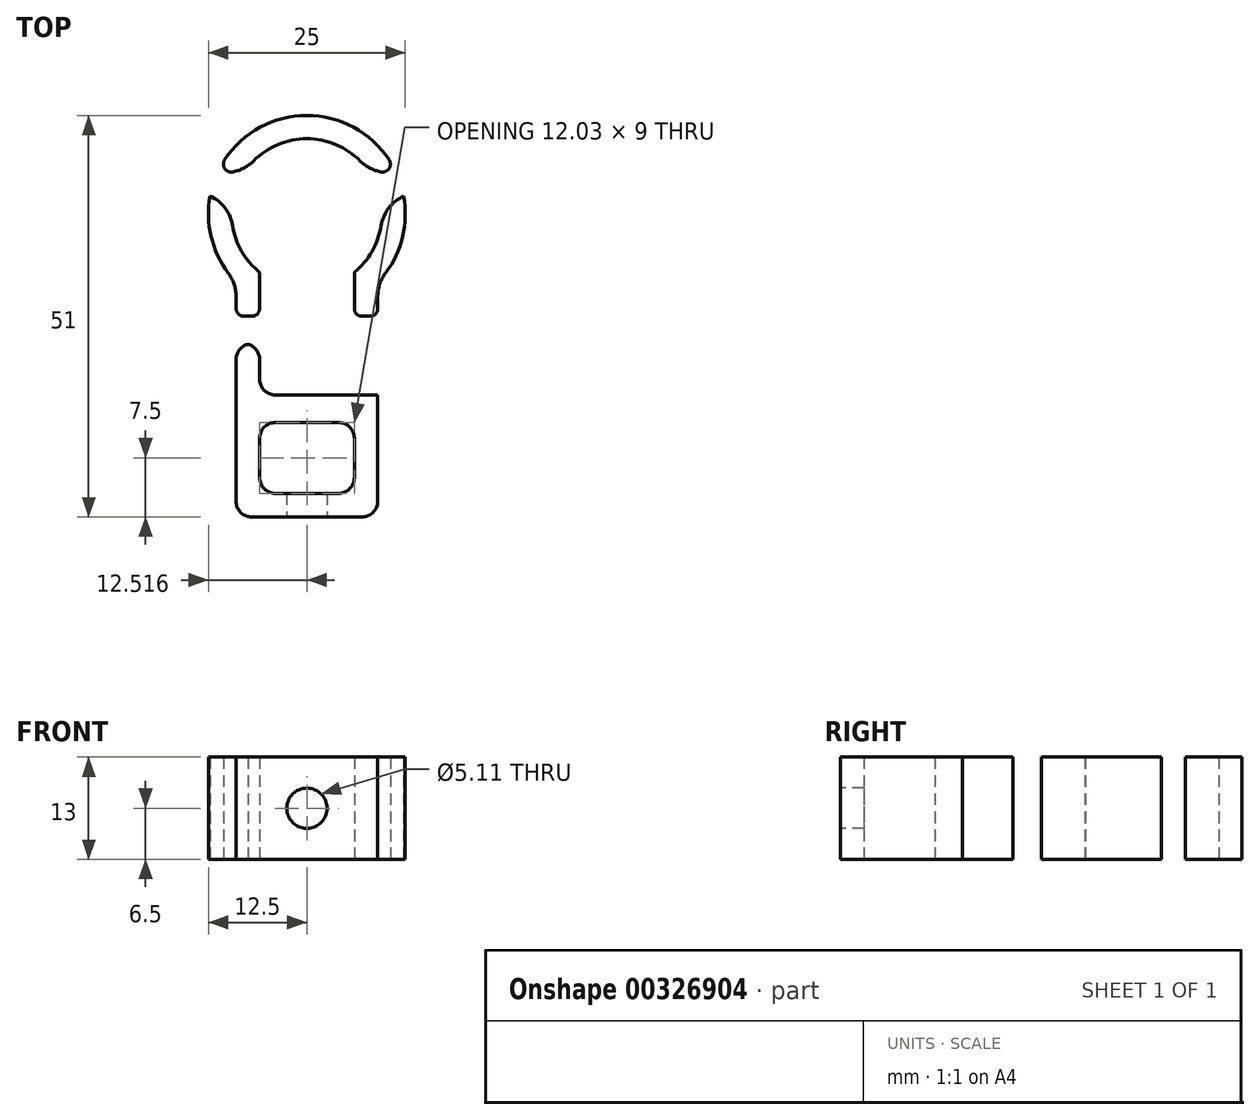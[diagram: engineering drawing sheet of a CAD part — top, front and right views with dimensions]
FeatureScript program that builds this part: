
annotation { "Feature Type Name" : "Feature", "Feature Type Description" : "" }
export const myFeature = defineFeature(function(context is Context, id is Id, definition is map)
    precondition{}
    {
        {
            var Q0;
            Q0=qCreatedBy(makeId("Top.planeOp"),FACE);
            var sketch = newSketch(context, id + "F0", { "sketchPlane" : qUnion([Q0])});
            skCircle(sketch, "E0", {"center": v(0, 0) * mm, "radius": 9.55 * mm});
            skCircle(sketch, "E1", {"center": v(0, 0) * mm, "radius": 12.5 * mm});
            skLineSegment(sketch, "E2", {"start": v(-6, -16.5) * mm, "end": v(-6, -10.97) * mm});
            skLineSegment(sketch, "E3", {"start": v(6.03, -16.54) * mm, "end": v(6.03, -10.95) * mm});
            skLineSegment(sketch, "E4", {"start": v(-12.3, 2.26) * mm, "end": v(12.3, 2.26) * mm});
            skLineSegment(sketch, "E5.0", {"start": v(-12.3, 5.26) * mm, "end": v(12.3, 5.26) * mm});
            skLineSegment(sketch, "E6", {"start": v(6.03, -10.95) * mm, "end": v(6.03, -7.4) * mm});
            skLineSegment(sketch, "E7", {"start": v(-6, -10.97) * mm, "end": v(-6, -7.43) * mm});
            skLineSegment(sketch, "E8", {"start": v(-6, -7.43) * mm, "end": v(-6, -16.5) * mm});
            skLineSegment(sketch, "E9", {"start": v(6.03, -7.4) * mm, "end": v(6.03, -16.54) * mm});
            skLineSegment(sketch, "E10.0", {"start": v(-9, -16.5) * mm, "end": v(-9, -10.97) * mm});
            skLineSegment(sketch, "E11", {"start": v(-9, -10.97) * mm, "end": v(-9, -8.67) * mm});
            skLineSegment(sketch, "E12", {"start": v(9, -16.5) * mm, "end": v(9, -8.67) * mm});
            skLineSegment(sketch, "E13", {"start": v(-9, -16.5) * mm, "end": v(9, -16.5) * mm});
            skLineSegment(sketch, "E14.0", {"start": v(-9, -13) * mm, "end": v(9, -13) * mm});
            skLineSegment(sketch, "E15", {"start": v(-6, -7.43) * mm, "end": v(6.03, -7.4) * mm});
            skLineSegment(sketch, "E16.0", {"start": v(-6.02, -6.43) * mm, "end": v(6.05, -6.4) * mm});
            skLineSegment(sketch, "E17", {"start": v(6.05, -6.4) * mm, "end": v(7.08, -6.4) * mm});
            skLineSegment(sketch, "E18", {"start": v(-6.02, -6.43) * mm, "end": v(-7.06, -6.43) * mm});
            skLineSegment(sketch, "E19.0", {"start": v(-9, -26.5) * mm, "end": v(9, -26.5) * mm});
            skLineSegment(sketch, "E20", {"start": v(-9, -16.5) * mm, "end": v(-9, -26.5) * mm});
            skLineSegment(sketch, "E21", {"start": v(9, -16.5) * mm, "end": v(9, -26.5) * mm});
            skLineSegment(sketch, "E22", {"start": v(6.03, -16.54) * mm, "end": v(6.03, -26.5) * mm});
            skLineSegment(sketch, "E23", {"start": v(-6, -16.5) * mm, "end": v(-6, -26.5) * mm});
            skLineSegment(sketch, "E24.0", {"start": v(-9, -23) * mm, "end": v(9, -23) * mm});
            skLineSegment(sketch, "E25.0", {"start": v(-9, -35.5) * mm, "end": v(9, -35.5) * mm});
            skLineSegment(sketch, "E26.0", {"start": v(-9, -38.5) * mm, "end": v(9, -38.5) * mm});
            skLineSegment(sketch, "E27", {"start": v(-9, -38.5) * mm, "end": v(-9, -26.5) * mm});
            skLineSegment(sketch, "E28", {"start": v(9, -38.5) * mm, "end": v(9, -26.5) * mm});
            skLineSegment(sketch, "E29", {"start": v(6.03, -26.5) * mm, "end": v(6.03, -35.5) * mm});
            skLineSegment(sketch, "E30", {"start": v(-6, -26.5) * mm, "end": v(-6, -35.5) * mm});
            skSolve(sketch);
        }
        {
            var Q0;
            {var subQ0=sQuery(id+"F0.wireOp",EDGE,"E5.0");var subQ1=sQuery(id+"F0.wireOp",EDGE,"E0");var subQ2=makeQuery(id+"F0.imprint","INTERSECT",VERTEX,{"disambiguationData":[OD(1.0)],"derivedFrom":[subQ1,subQ0]});Q0=makeQuery(id+"F0.imprint","IMPRINT",FACE,{"disambiguationData":[TD([[makeQuery(id+"F0.imprint","IMPRINT",EDGE,{"disambiguationData":[TD([[subQ2,-1.0]])],"derivedFrom":subQ1}),-1.0]])]});}
            var Q1;
            {var subQ2=sQuery(id+"F0.wireOp",EDGE,"E8");var subQ6=sQuery(id+"F0.wireOp",EDGE,"E0");var subQ8=makeQuery(id+"F0.imprint","INTERSECT",VERTEX,{"derivedFrom":[subQ6,subQ2]});Q1=makeQuery(id+"F0.imprint","IMPRINT",FACE,{"disambiguationData":[TD([[makeQuery(id+"F0.imprint","IMPRINT",EDGE,{"disambiguationData":[TD([[subQ8,1.0]])],"derivedFrom":subQ6}),-1.0]])]});}
            var Q2;
            {var subQ0=sQuery(id+"F0.wireOp",EDGE,"E5.0");var subQ1=sQuery(id+"F0.wireOp",EDGE,"E0");var subQ2=makeQuery(id+"F0.imprint","INTERSECT",VERTEX,{"disambiguationData":[OD(0.0)],"derivedFrom":[subQ1,subQ0]});Q2=makeQuery(id+"F0.imprint","IMPRINT",FACE,{"disambiguationData":[TD([[makeQuery(id+"F0.imprint","IMPRINT",EDGE,{"disambiguationData":[TD([[subQ2,1.0]])],"derivedFrom":subQ1}),-1.0]])]});}
            var Q3;
            {var subQ3=sQuery(id+"F0.wireOp",EDGE,"E0");var subQ5=sQuery(id+"F0.wireOp",EDGE,"E9");var subQ6=makeQuery(id+"F0.imprint","INTERSECT",VERTEX,{"derivedFrom":[subQ3,subQ5]});Q3=makeQuery(id+"F0.imprint","IMPRINT",FACE,{"disambiguationData":[TD([[makeQuery(id+"F0.imprint","IMPRINT",EDGE,{"disambiguationData":[TD([[subQ6,-1.0]])],"derivedFrom":subQ3}),-1.0]])]});}
            var Q4;
            {var subQ0=sQuery(id+"F0.wireOp",EDGE,"E12");var subQ1=sQuery(id+"F0.wireOp",EDGE,"E1");var subQ2=makeQuery(id+"F0.imprint","INTERSECT",VERTEX,{"derivedFrom":[subQ1,subQ0]});Q4=makeQuery(id+"F0.imprint","IMPRINT",FACE,{"disambiguationData":[TD([[makeQuery(id+"F0.imprint","IMPRINT",EDGE,{"disambiguationData":[TD([[subQ2,1.0]])],"derivedFrom":subQ1}),-1.0]])]});}
            var Q5;
            {var subQ0=sQuery(id+"F0.wireOp",EDGE,"E13");var subQ1=sQuery(id+"F0.wireOp",EDGE,"E9");var subQ2=makeQuery(id+"F0.imprint","INTERSECT",VERTEX,{"derivedFrom":[subQ1,subQ0]});Q5=makeQuery(id+"F0.imprint","IMPRINT",FACE,{"disambiguationData":[TD([[makeQuery(id+"F0.imprint","IMPRINT",EDGE,{"disambiguationData":[TD([[subQ2,1.0]])],"derivedFrom":subQ1}),1.0]])]});}
            var Q6;
            {var subQ0=sQuery(id+"F0.wireOp",EDGE,"E13");var subQ1=sQuery(id+"F0.wireOp",EDGE,"E8");var subQ2=makeQuery(id+"F0.imprint","INTERSECT",VERTEX,{"derivedFrom":[subQ1,subQ0]});Q6=makeQuery(id+"F0.imprint","IMPRINT",FACE,{"disambiguationData":[TD([[makeQuery(id+"F0.imprint","IMPRINT",EDGE,{"disambiguationData":[TD([[subQ2,1.0]])],"derivedFrom":subQ1}),1.0]])]});}
            var Q7;
            {var subQ0=sQuery(id+"F0.wireOp",EDGE,"E13");var subQ1=sQuery(id+"F0.wireOp",EDGE,"E8");var subQ2=makeQuery(id+"F0.imprint","INTERSECT",VERTEX,{"derivedFrom":[subQ1,subQ0]});Q7=makeQuery(id+"F0.imprint","IMPRINT",FACE,{"disambiguationData":[TD([[makeQuery(id+"F0.imprint","IMPRINT",EDGE,{"disambiguationData":[TD([[subQ2,1.0]])],"derivedFrom":subQ1}),-1.0]])]});}
            var Q8;
            {var subQ0=sQuery(id+"F0.wireOp",EDGE,"E11");Q8=makeQuery(id+"F0.imprint","IMPRINT",FACE,{"disambiguationData":[TD([[makeQuery(id+"F0.imprint","IMPRINT",EDGE,{"derivedFrom":subQ0}),-1.0]])]});}
            extrude(context, id + "F1", {"entities" : qUnion([Q0, Q1, Q2, Q3, Q4, Q5, Q6, Q7, Q8]), "depth" : 13 * mm});
        }
        {
            var Q0;
            Q0=makeQuery(id+"F1.opExtrude","SWEPT_EDGE",EDGE,{"disambiguationData":[OSD([sQuery(id+"F0.wireOp",EDGE,"E1"),sQuery(id+"F0.wireOp",EDGE,"E12")])]});
            var Q1;
            Q1=makeQuery(id+"F1.opExtrude","SWEPT_EDGE",EDGE,{"disambiguationData":[OSD([sQuery(id+"F0.wireOp",EDGE,"E1"),sQuery(id+"F0.wireOp",EDGE,"E11")])]});
            var Q2;
            Q2=makeQuery(id+"F1.opExtrude","SWEPT_EDGE",EDGE,{"disambiguationData":[OSD([sQuery(id+"F0.wireOp",EDGE,"E0"),sQuery(id+"F0.wireOp",EDGE,"E9")])]});
            var Q3;
            Q3=makeQuery(id+"F1.opExtrude","SWEPT_EDGE",EDGE,{"disambiguationData":[OSD([sQuery(id+"F0.wireOp",EDGE,"E0"),sQuery(id+"F0.wireOp",EDGE,"E8")])]});
            fillet(context, id + "F2", {"entities" : qUnion([Q0, Q1, Q2, Q3]), "radius" : 5 * mm, "tangentPropagation" : true, "allowEdgeOverflow" : false});
        }
        {
            var Q0;
            {var subQ0=sQuery(id+"F0.wireOp",EDGE,"E5.0");var subQ1=sQuery(id+"F0.wireOp",EDGE,"E1");Q0=makeQuery(id+"F1.opExtrude","SWEPT_EDGE",EDGE,{"disambiguationData":[OSD([subQ1,subQ0]),TDD([makeQuery(id+"F0.imprint","INTERSECT",VERTEX,{"disambiguationData":[OD(1.0)],"derivedFrom":[subQ1,subQ0]})])]});}
            var Q1;
            {var subQ0=sQuery(id+"F0.wireOp",EDGE,"E5.0");var subQ1=sQuery(id+"F0.wireOp",EDGE,"E0");Q1=makeQuery(id+"F1.opExtrude","SWEPT_EDGE",EDGE,{"disambiguationData":[OSD([subQ1,subQ0]),TDD([makeQuery(id+"F0.imprint","INTERSECT",VERTEX,{"disambiguationData":[OD(0.0)],"derivedFrom":[subQ1,subQ0]})])]});}
            var Q2;
            {var subQ0=sQuery(id+"F0.wireOp",EDGE,"E5.0");var subQ1=sQuery(id+"F0.wireOp",EDGE,"E0");Q2=makeQuery(id+"F1.opExtrude","SWEPT_EDGE",EDGE,{"disambiguationData":[OSD([subQ1,subQ0]),TDD([makeQuery(id+"F0.imprint","INTERSECT",VERTEX,{"disambiguationData":[OD(1.0)],"derivedFrom":[subQ1,subQ0]})])]});}
            var Q3;
            {var subQ0=sQuery(id+"F0.wireOp",EDGE,"E5.0");var subQ1=sQuery(id+"F0.wireOp",EDGE,"E1");Q3=makeQuery(id+"F1.opExtrude","SWEPT_EDGE",EDGE,{"disambiguationData":[OSD([subQ1,subQ0]),TDD([makeQuery(id+"F0.imprint","INTERSECT",VERTEX,{"disambiguationData":[OD(0.0)],"derivedFrom":[subQ1,subQ0]})])]});}
            var Q4;
            Q4=makeQuery(id+"F1.opExtrude","SWEPT_EDGE",EDGE,{"disambiguationData":[OSD([sQuery(id+"F0.wireOp",EDGE,"E8"),sQuery(id+"F0.wireOp",EDGE,"E14.0")])]});
            var Q5;
            Q5=makeQuery(id+"F1.opExtrude","SWEPT_EDGE",EDGE,{"disambiguationData":[OSD([sQuery(id+"F0.wireOp",EDGE,"E9"),sQuery(id+"F0.wireOp",EDGE,"E14.0")])]});
            fillet(context, id + "F3", {"entities" : qUnion([Q0, Q1, Q2, Q3, Q4, Q5]), "radius" : 1 * mm, "tangentPropagation" : true, "allowEdgeOverflow" : false});
        }
        {
            var Q0;
            Q0=makeQuery(id+"F1.opExtrude","SWEPT_FACE",FACE,{"disambiguationData":[OSD([sQuery(id+"F0.wireOp",EDGE,"E13")])]});
            var sketch = newSketch(context, id + "F4", { "sketchPlane" : qUnion([Q0])});
            skLineSegment(sketch, "E31", {"start": v(0, 0) * mm, "end": v(0, 13) * mm, "construction": true});
            skCircle(sketch, "E32", {"center": v(0, 6.5) * mm, "radius": 2.55 * mm});
            skSolve(sketch);
        }
        {
            var Q0;
            Q0=makeQuery(id+"F1.opExtrude","SWEPT_BODY",BODY,{"disambiguationData":[OSD([sQuery(id+"F0.wireOp",EDGE,"E0"),sQuery(id+"F0.wireOp",EDGE,"E1"),sQuery(id+"F0.wireOp",EDGE,"E5.0"),sQuery(id+"F0.wireOp",EDGE,"E8"),sQuery(id+"F0.wireOp",EDGE,"E9"),sQuery(id+"F0.wireOp",EDGE,"E10.0"),sQuery(id+"F0.wireOp",EDGE,"E11"),sQuery(id+"F0.wireOp",EDGE,"E12"),sQuery(id+"F0.wireOp",EDGE,"E13"),sQuery(id+"F0.wireOp",EDGE,"E14.0")])]});
            transform(context, id + "F5", {"entities" : qUnion([Q0]), "transformType" : TransformType.TRANSLATION_3D, "dx" : 0 * mm, "dy" : 0 * mm, "dz" : 0 * mm, "makeCopy" : true});
        }
        {
            var Q0;
            Q0=makeQuery(id+"F1.opExtrude","SWEPT_BODY",BODY,{"disambiguationData":[OSD([sQuery(id+"F0.wireOp",EDGE,"E0"),sQuery(id+"F0.wireOp",EDGE,"E1"),sQuery(id+"F0.wireOp",EDGE,"E5.0"),sQuery(id+"F0.wireOp",EDGE,"E8"),sQuery(id+"F0.wireOp",EDGE,"E9"),sQuery(id+"F0.wireOp",EDGE,"E10.0"),sQuery(id+"F0.wireOp",EDGE,"E11"),sQuery(id+"F0.wireOp",EDGE,"E12"),sQuery(id+"F0.wireOp",EDGE,"E13"),sQuery(id+"F0.wireOp",EDGE,"E14.0")])]});
            transform(context, id + "F6", {"entities" : qUnion([Q0]), "transformType" : TransformType.TRANSLATION_3D, "dx" : 0 * mm, "dy" : 0 * mm, "dz" : 0 * mm, "makeCopy" : true});
        }
        {
            var Q0;
            Q0=makeQuery(id+"F5.opPattern","COPY",BODY,{"derivedFrom":makeQuery(id+"F1.opExtrude","SWEPT_BODY",BODY,{"disambiguationData":[OSD([sQuery(id+"F0.wireOp",EDGE,"E0"),sQuery(id+"F0.wireOp",EDGE,"E1"),sQuery(id+"F0.wireOp",EDGE,"E5.0"),sQuery(id+"F0.wireOp",EDGE,"E8"),sQuery(id+"F0.wireOp",EDGE,"E9"),sQuery(id+"F0.wireOp",EDGE,"E10.0"),sQuery(id+"F0.wireOp",EDGE,"E11"),sQuery(id+"F0.wireOp",EDGE,"E12"),sQuery(id+"F0.wireOp",EDGE,"E13"),sQuery(id+"F0.wireOp",EDGE,"E14.0")])]}),"instanceName":"1"});
            deleteBodies(context, id + "F7", {"entities" : qUnion([Q0])});
        }
        {
            var Q0;
            Q0=makeQuery(id+"F6.opPattern","COPY",BODY,{"derivedFrom":makeQuery(id+"F1.opExtrude","SWEPT_BODY",BODY,{"disambiguationData":[OSD([sQuery(id+"F0.wireOp",EDGE,"E0"),sQuery(id+"F0.wireOp",EDGE,"E1"),sQuery(id+"F0.wireOp",EDGE,"E5.0"),sQuery(id+"F0.wireOp",EDGE,"E8"),sQuery(id+"F0.wireOp",EDGE,"E9"),sQuery(id+"F0.wireOp",EDGE,"E10.0"),sQuery(id+"F0.wireOp",EDGE,"E11"),sQuery(id+"F0.wireOp",EDGE,"E12"),sQuery(id+"F0.wireOp",EDGE,"E13"),sQuery(id+"F0.wireOp",EDGE,"E14.0")])]}),"instanceName":"1"});
            deleteBodies(context, id + "F8", {"entities" : qUnion([Q0])});
        }
        {
            var Q0;
            {var subQ3=sQuery(id+"F0.wireOp",EDGE,"E20");var subQ5=sQuery(id+"F0.wireOp",EDGE,"E24.0");var subQ6=makeQuery(id+"F0.imprint","INTERSECT",VERTEX,{"derivedFrom":[subQ3,subQ5]});Q0=makeQuery(id+"F0.imprint","IMPRINT",FACE,{"disambiguationData":[TD([[makeQuery(id+"F0.imprint","IMPRINT",EDGE,{"disambiguationData":[TD([[subQ6,-1.0]])],"derivedFrom":subQ5}),1.0]])]});}
            var Q1;
            {var subQ0=sQuery(id+"F0.wireOp",EDGE,"E20");var subQ1=sQuery(id+"F0.wireOp",EDGE,"E19.0");var subQ2=makeQuery(id+"F0.imprint","INTERSECT",VERTEX,{"derivedFrom":[subQ1,subQ0]});Q1=makeQuery(id+"F0.imprint","IMPRINT",FACE,{"disambiguationData":[TD([[makeQuery(id+"F0.imprint","IMPRINT",EDGE,{"disambiguationData":[TD([[subQ2,-1.0]])],"derivedFrom":subQ1}),1.0]])]});}
            var Q2;
            {var subQ0=sQuery(id+"F0.wireOp",EDGE,"E22");var subQ1=sQuery(id+"F0.wireOp",EDGE,"E19.0");var subQ2=makeQuery(id+"F0.imprint","INTERSECT",VERTEX,{"derivedFrom":[subQ1,subQ0]});Q2=makeQuery(id+"F0.imprint","IMPRINT",FACE,{"disambiguationData":[TD([[makeQuery(id+"F0.imprint","IMPRINT",EDGE,{"disambiguationData":[TD([[subQ2,1.0]])],"derivedFrom":subQ1}),1.0]])]});}
            var Q3;
            {var subQ0=sQuery(id+"F0.wireOp",EDGE,"E21");var subQ1=sQuery(id+"F0.wireOp",EDGE,"E19.0");var subQ2=makeQuery(id+"F0.imprint","INTERSECT",VERTEX,{"derivedFrom":[subQ1,subQ0]});Q3=makeQuery(id+"F0.imprint","IMPRINT",FACE,{"disambiguationData":[TD([[makeQuery(id+"F0.imprint","IMPRINT",EDGE,{"disambiguationData":[TD([[subQ2,1.0]])],"derivedFrom":subQ1}),1.0]])]});}
            var Q4;
            {var subQ5=sQuery(id+"F0.wireOp",EDGE,"E22");var subQ6=sQuery(id+"F0.wireOp",EDGE,"E9");var subQ7=makeQuery(id+"F0.imprint","INTERSECT",VERTEX,{"derivedFrom":[subQ6,subQ5]});Q4=makeQuery(id+"F0.imprint","IMPRINT",FACE,{"disambiguationData":[TD([[makeQuery(id+"F0.imprint","IMPRINT",EDGE,{"disambiguationData":[TD([[subQ7,1.0]])],"derivedFrom":subQ6}),1.0]])]});}
            extrude(context, id + "F9", {"entities" : qUnion([Q0, Q1, Q2, Q3, Q4]), "operationType" : NewBodyOperationType.ADD, "depth" : 13 * mm});
        }
        {
            var Q0;
            Q0=makeQuery(id+"F9.opExtrude","SWEPT_EDGE",EDGE,{"disambiguationData":[OSD([sQuery(id+"F0.wireOp",EDGE,"E22"),sQuery(id+"F0.wireOp",EDGE,"E24.0")])]});
            var Q1;
            Q1=makeQuery(id+"F9.opExtrude","SWEPT_EDGE",EDGE,{"disambiguationData":[OSD([sQuery(id+"F0.wireOp",EDGE,"E9"),sQuery(id+"F0.wireOp",EDGE,"E13")])]});
            var Q2;
            Q2=makeQuery(id+"F9.opExtrude","SWEPT_EDGE",EDGE,{"disambiguationData":[OSD([sQuery(id+"F0.wireOp",EDGE,"E8"),sQuery(id+"F0.wireOp",EDGE,"E13"),sQuery(id+"F0.wireOp",EDGE,"E23")])]});
            var Q3;
            Q3=makeQuery(id+"F9.opExtrude","SWEPT_EDGE",EDGE,{"disambiguationData":[OSD([sQuery(id+"F0.wireOp",EDGE,"E23"),sQuery(id+"F0.wireOp",EDGE,"E24.0")])]});
            fillet(context, id + "F10", {"entities" : qUnion([Q0, Q1, Q2, Q3]), "radius" : 2 * mm, "tangentPropagation" : true, "allowEdgeOverflow" : false});
        }
        {
            var Q0;
            {var subQ0=sQuery(id+"F0.wireOp",EDGE,"E21");var subQ5=sQuery(id+"F0.wireOp",EDGE,"E24.0");var subQ6=makeQuery(id+"F0.imprint","INTERSECT",VERTEX,{"derivedFrom":[subQ0,subQ5]});Q0=makeQuery(id+"F0.imprint","IMPRINT",FACE,{"disambiguationData":[TD([[makeQuery(id+"F0.imprint","IMPRINT",EDGE,{"disambiguationData":[TD([[subQ6,1.0]])],"derivedFrom":subQ5}),-1.0]])]});}
            var Q1;
            {var subQ0=sQuery(id+"F0.wireOp",EDGE,"E20");var subQ5=sQuery(id+"F0.wireOp",EDGE,"E24.0");var subQ7=makeQuery(id+"F0.imprint","INTERSECT",VERTEX,{"derivedFrom":[subQ0,subQ5]});Q1=makeQuery(id+"F0.imprint","IMPRINT",FACE,{"disambiguationData":[TD([[makeQuery(id+"F0.imprint","IMPRINT",EDGE,{"disambiguationData":[TD([[subQ7,-1.0]])],"derivedFrom":subQ5}),-1.0]])]});}
            var Q2;
            {var subQ3=sQuery(id+"F0.wireOp",EDGE,"E30");Q2=makeQuery(id+"F0.imprint","IMPRINT",FACE,{"disambiguationData":[TD([[makeQuery(id+"F0.imprint","IMPRINT",EDGE,{"derivedFrom":subQ3}),-1.0]])]});}
            var Q3;
            {var subQ3=sQuery(id+"F0.wireOp",EDGE,"E29");Q3=makeQuery(id+"F0.imprint","IMPRINT",FACE,{"disambiguationData":[TD([[makeQuery(id+"F0.imprint","IMPRINT",EDGE,{"derivedFrom":subQ3}),1.0]])]});}
            var Q4;
            {var subQ0=sQuery(id+"F0.wireOp",EDGE,"E26.0");Q4=makeQuery(id+"F0.imprint","IMPRINT",FACE,{"disambiguationData":[TD([[makeQuery(id+"F0.imprint","IMPRINT",EDGE,{"derivedFrom":subQ0}),1.0]])]});}
            extrude(context, id + "F11", {"entities" : qUnion([Q0, Q1, Q2, Q3, Q4]), "operationType" : NewBodyOperationType.ADD, "depth" : 13 * mm});
        }
        {
            var Q0;
            Q0=makeQuery(id+"F11.boolean.opBoolean","INTERSECT",EDGE,{"derivedFrom":[makeQuery(id+"F9.opExtrude","SWEPT_FACE",FACE,{"disambiguationData":[OSD([sQuery(id+"F0.wireOp",EDGE,"E19.0")])]}),makeQuery(id+"F11.opExtrude","SWEPT_FACE",FACE,{"disambiguationData":[OSD([sQuery(id+"F0.wireOp",EDGE,"E23"),sQuery(id+"F0.wireOp",EDGE,"E30")])]})]});
            var Q1;
            Q1=makeQuery(id+"F11.boolean.opBoolean","INTERSECT",EDGE,{"derivedFrom":[makeQuery(id+"F9.opExtrude","SWEPT_FACE",FACE,{"disambiguationData":[OSD([sQuery(id+"F0.wireOp",EDGE,"E19.0")])]}),makeQuery(id+"F11.opExtrude","SWEPT_FACE",FACE,{"disambiguationData":[OSD([sQuery(id+"F0.wireOp",EDGE,"E22"),sQuery(id+"F0.wireOp",EDGE,"E29")])]})]});
            var Q2;
            Q2=makeQuery(id+"F11.opExtrude","SWEPT_EDGE",EDGE,{"disambiguationData":[OSD([sQuery(id+"F0.wireOp",EDGE,"E26.0"),sQuery(id+"F0.wireOp",EDGE,"E27")])]});
            var Q3;
            Q3=makeQuery(id+"F11.opExtrude","SWEPT_EDGE",EDGE,{"disambiguationData":[OSD([sQuery(id+"F0.wireOp",EDGE,"E26.0"),sQuery(id+"F0.wireOp",EDGE,"E28")])]});
            var Q4;
            Q4=makeQuery(id+"F11.opExtrude","SWEPT_EDGE",EDGE,{"disambiguationData":[OSD([sQuery(id+"F0.wireOp",EDGE,"E25.0"),sQuery(id+"F0.wireOp",EDGE,"E30")])]});
            var Q5;
            Q5=makeQuery(id+"F11.opExtrude","SWEPT_EDGE",EDGE,{"disambiguationData":[OSD([sQuery(id+"F0.wireOp",EDGE,"E25.0"),sQuery(id+"F0.wireOp",EDGE,"E29")])]});
            fillet(context, id + "F12", {"entities" : qUnion([Q0, Q1, Q2, Q3, Q4, Q5]), "radius" : 2 * mm, "tangentPropagation" : true, "allowEdgeOverflow" : false});
        }
        {
            var Q0;
            Q0=makeQuery(id+"F11.opExtrude","SWEPT_FACE",FACE,{"disambiguationData":[OSD([sQuery(id+"F0.wireOp",EDGE,"E26.0")])]});
            var sketch = newSketch(context, id + "F13", { "sketchPlane" : qUnion([Q0])});
            skCircle(sketch, "E33.0", {"center": v(0, 6.5) * mm, "radius": 2.55 * mm});
            skLineSegment(sketch, "E34.0.0", {"start": v(-7, 0) * mm, "end": v(7, 0) * mm});
            skLineSegment(sketch, "E34.0.1", {"start": v(7, 0) * mm, "end": v(7, 13) * mm});
            skLineSegment(sketch, "E34.0.2", {"start": v(7, 13) * mm, "end": v(-7, 13) * mm});
            skLineSegment(sketch, "E34.0.3", {"start": v(-7, 13) * mm, "end": v(-7, 0) * mm});
            skSolve(sketch);
        }
        {
            var Q0;
            Q0=makeQuery(id+"F13.imprint","IMPRINT",FACE,{"disambiguationData":[TD([[makeQuery(id+"F13.imprint","IMPRINT",EDGE,{"derivedFrom":sQuery(id+"F13.wireOp",EDGE,"E33.0")}),1.0]])]});
            extrude(context, id + "F14", {"entities" : qUnion([Q0]), "operationType" : NewBodyOperationType.REMOVE, "oppositeDirection" : true, "depth" : 5 * mm, "offsetDistance" : 25 * mm});
        }
    });
